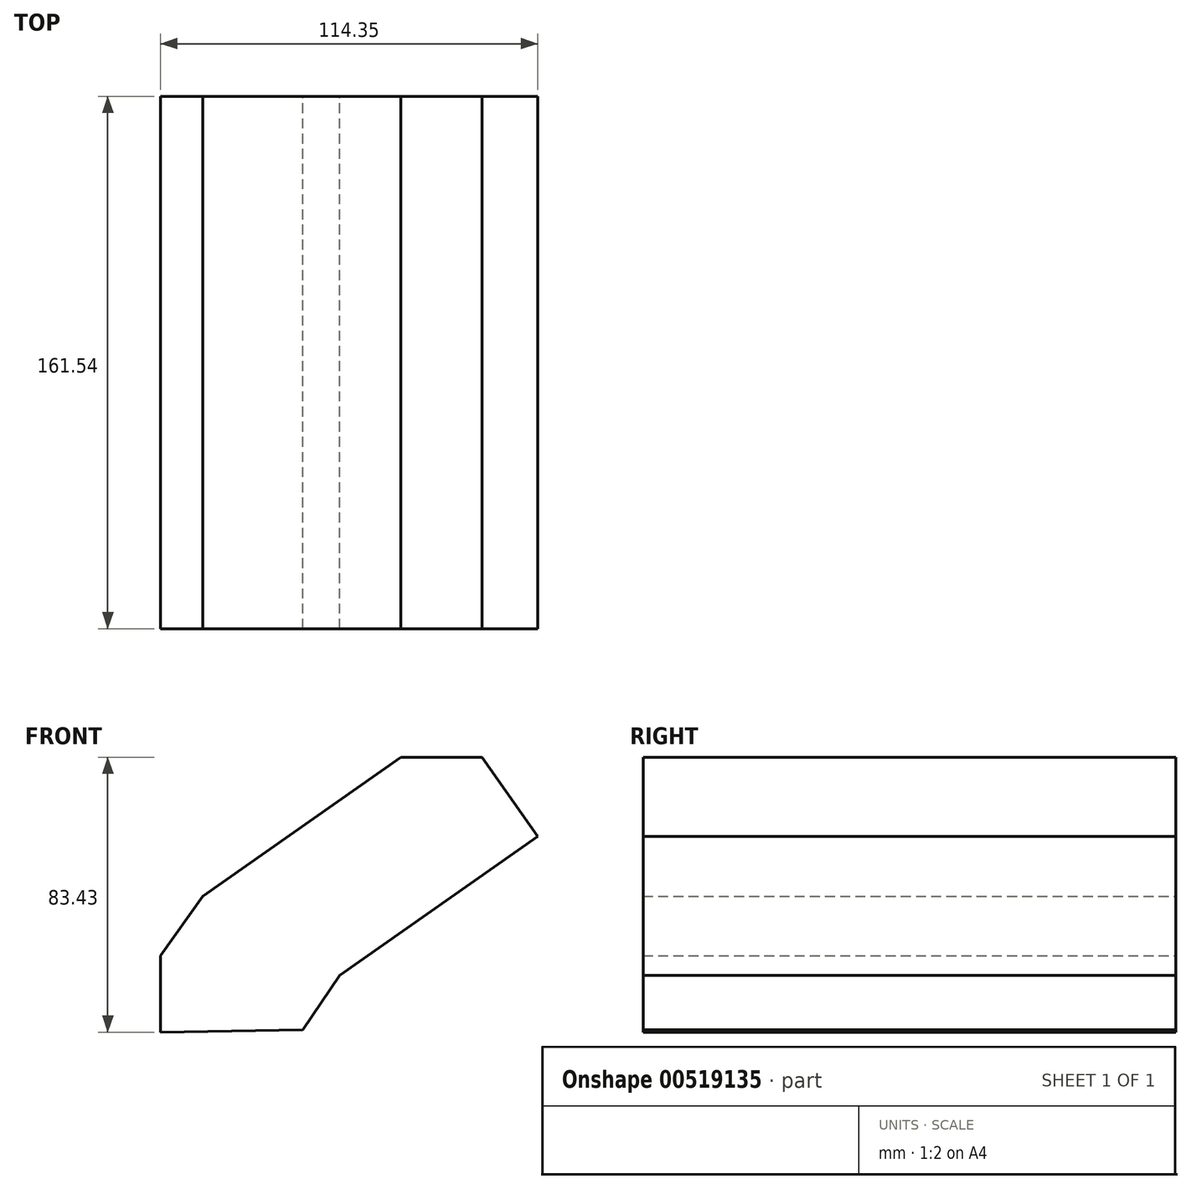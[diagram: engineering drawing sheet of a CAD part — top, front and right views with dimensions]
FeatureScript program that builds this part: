
annotation { "Feature Type Name" : "Feature", "Feature Type Description" : "" }
export const myFeature = defineFeature(function(context is Context, id is Id, definition is map)
    precondition{}
    {
        {
            var Q0;
            Q0=qCreatedBy(makeId("Front.planeOp"),FACE);
            var sketch = newSketch(context, id + "F0", { "sketchPlane" : qUnion([Q0])});
            skLineSegment(sketch, "E0", {"start": v(0, 0) * mm, "end": v(-26.1, -18.32) * mm});
            skLineSegment(sketch, "E1", {"start": v(-26.1, -18.32) * mm, "end": v(-7.38, -45) * mm});
            skLineSegment(sketch, "E2", {"start": v(-7.38, -45) * mm, "end": v(13.2, -34.49) * mm});
            skLineSegment(sketch, "E3", {"start": v(13.2, -34.49) * mm, "end": v(5.99, -20.4) * mm});
            skLineSegment(sketch, "E4", {"start": v(5.99, -20.4) * mm, "end": v(22.66, -11.88) * mm});
            skLineSegment(sketch, "E5", {"start": v(22.66, -11.88) * mm, "end": v(0, 0) * mm});
            skLineSegment(sketch, "E6", {"start": v(0, 0) * mm, "end": v(16.54, 0) * mm});
            skLineSegment(sketch, "E7", {"start": v(16.54, 0) * mm, "end": v(28.15, 17.23) * mm});
            skLineSegment(sketch, "E8", {"start": v(28.15, 17.23) * mm, "end": v(11.29, 41.26) * mm});
            skLineSegment(sketch, "E9", {"start": v(11.29, 41.26) * mm, "end": v(-13.37, 41.26) * mm});
            skLineSegment(sketch, "E10", {"start": v(-13.37, 41.26) * mm, "end": v(-26.1, 23.2) * mm});
            skLineSegment(sketch, "E11", {"start": v(-26.1, 23.2) * mm, "end": v(-26.1, 0) * mm});
            skLineSegment(sketch, "E12", {"start": v(-26.1, 0) * mm, "end": v(17.04, 0.75) * mm});
            skSolve(sketch);
        }
        {
            var Q0;
            {var subQ0=sQuery(id+"F0.wireOp",EDGE,"E8");Q0=makeQuery(id+"F0.imprint","IMPRINT",FACE,{"disambiguationData":[TD([[makeQuery(id+"F0.imprint","IMPRINT",EDGE,{"derivedFrom":subQ0}),1.0]])]});}
            extrude(context, id + "F1", {"entities" : qUnion([Q0]), "depth" : 161.54 * mm});
        }
        {
            var Q0;
            Q0=makeQuery(id+"F1.opExtrude","SWEPT_FACE",FACE,{"disambiguationData":[OSD([sQuery(id+"F0.wireOp",EDGE,"E8")])]});
            var Q1;
            Q1=makeQuery(id+"F1.opExtrude","SWEPT_FACE",FACE,{"disambiguationData":[OSD([sQuery(id+"F0.wireOp",EDGE,"E9")])]});
            extrude(context, id + "F2", {"entities" : qUnion([Q0, Q1]), "operationType" : NewBodyOperationType.ADD, "depth" : 73.4 * mm});
        }
    });
